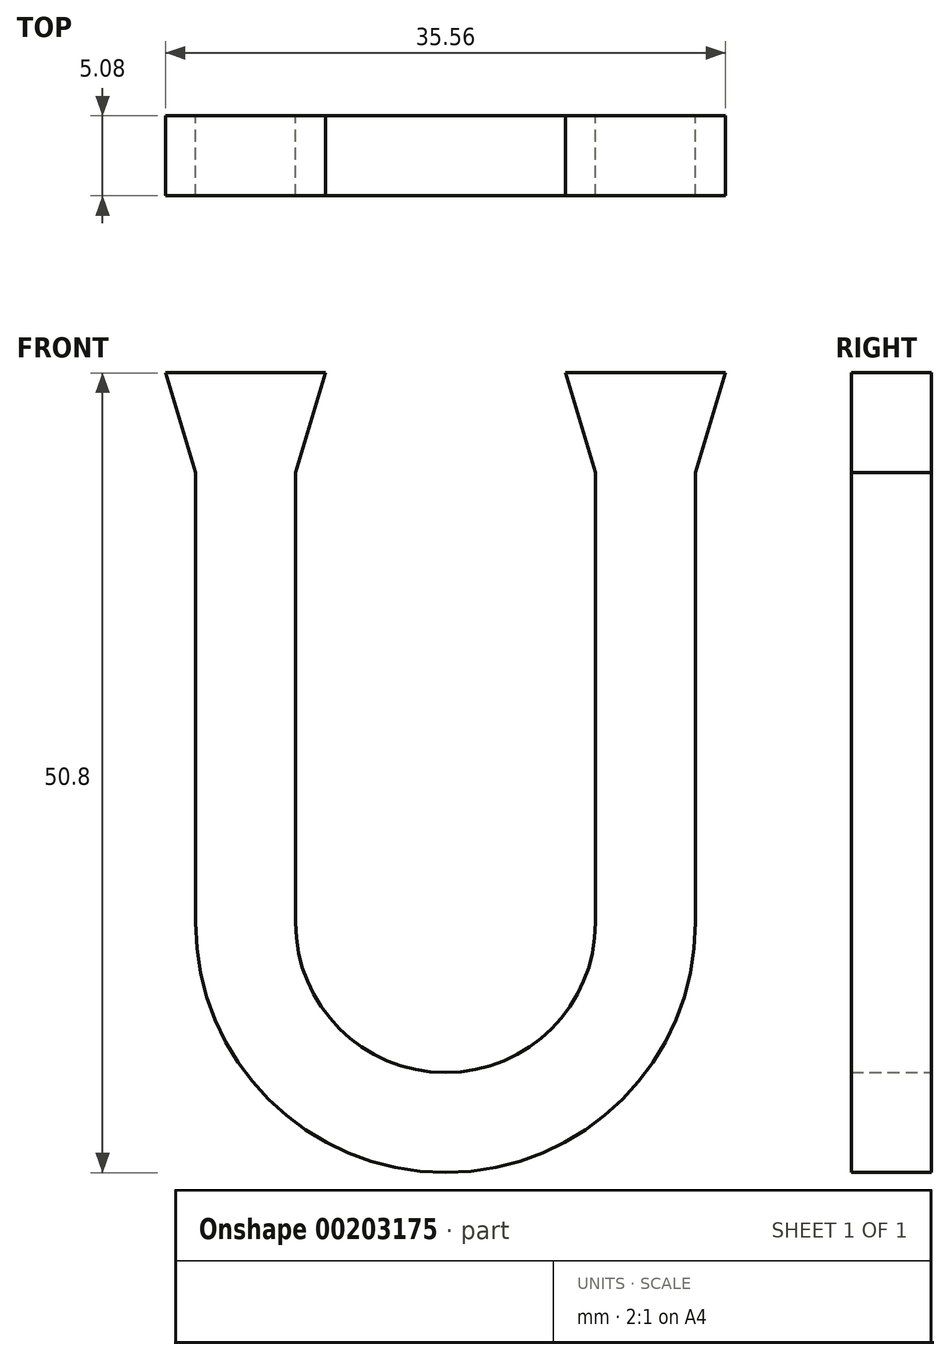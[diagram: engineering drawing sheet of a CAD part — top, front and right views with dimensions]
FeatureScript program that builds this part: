
annotation { "Feature Type Name" : "Feature", "Feature Type Description" : "" }
export const myFeature = defineFeature(function(context is Context, id is Id, definition is map)
    precondition{}
    {
        {
            var Q0;
            Q0=qCreatedBy(makeId("Front.planeOp"),FACE);
            var sketch = newSketch(context, id + "F0", { "sketchPlane" : qUnion([Q0])});
            skArc(sketch, "E0", {"start": v(-15.88, 0) * mm, "mid": v(0, -15.88) * mm, "end": v(15.88, 0) * mm});
            skLineSegment(sketch, "E1.top", {"start": v(-15.88, 34.92) * mm, "end": v(-9.52, 34.92) * mm});
            skLineSegment(sketch, "E1.left", {"start": v(-15.88, 0) * mm, "end": v(-15.88, 28.58) * mm});
            skLineSegment(sketch, "E1.right", {"start": v(-9.53, 0) * mm, "end": v(-9.52, 28.58) * mm});
            skLineSegment(sketch, "E2.top", {"start": v(15.87, 34.92) * mm, "end": v(9.52, 34.92) * mm});
            skLineSegment(sketch, "E2.left", {"start": v(15.88, 0) * mm, "end": v(15.87, 28.57) * mm});
            skLineSegment(sketch, "E2.right", {"start": v(9.52, 0) * mm, "end": v(9.52, 28.58) * mm});
            skArc(sketch, "E3", {"start": v(-9.53, 0) * mm, "mid": v(0, -9.53) * mm, "end": v(9.53, 0) * mm});
            skLineSegment(sketch, "E4", {"start": v(-15.87, 28.58) * mm, "end": v(-17.78, 34.93) * mm});
            skLineSegment(sketch, "E5", {"start": v(-17.78, 34.92) * mm, "end": v(-15.88, 34.92) * mm});
            skLineSegment(sketch, "E6", {"start": v(-9.52, 34.92) * mm, "end": v(-7.62, 34.92) * mm});
            skLineSegment(sketch, "E7", {"start": v(-7.62, 34.93) * mm, "end": v(-9.53, 28.58) * mm});
            skLineSegment(sketch, "E8", {"start": v(9.52, 34.92) * mm, "end": v(7.62, 34.92) * mm});
            skLineSegment(sketch, "E9", {"start": v(7.62, 34.92) * mm, "end": v(9.52, 28.58) * mm});
            skLineSegment(sketch, "E10", {"start": v(15.87, 34.92) * mm, "end": v(17.78, 34.92) * mm});
            skLineSegment(sketch, "E11", {"start": v(17.78, 34.92) * mm, "end": v(15.88, 28.57) * mm});
            skSolve(sketch);
        }
        {
            var Q0;
            Q0=qSketchRegion(id+"F0",true);
            extrude(context, id + "F1", {"entities" : qUnion([Q0]), "depth" : 5.08 * mm});
        }
    });
